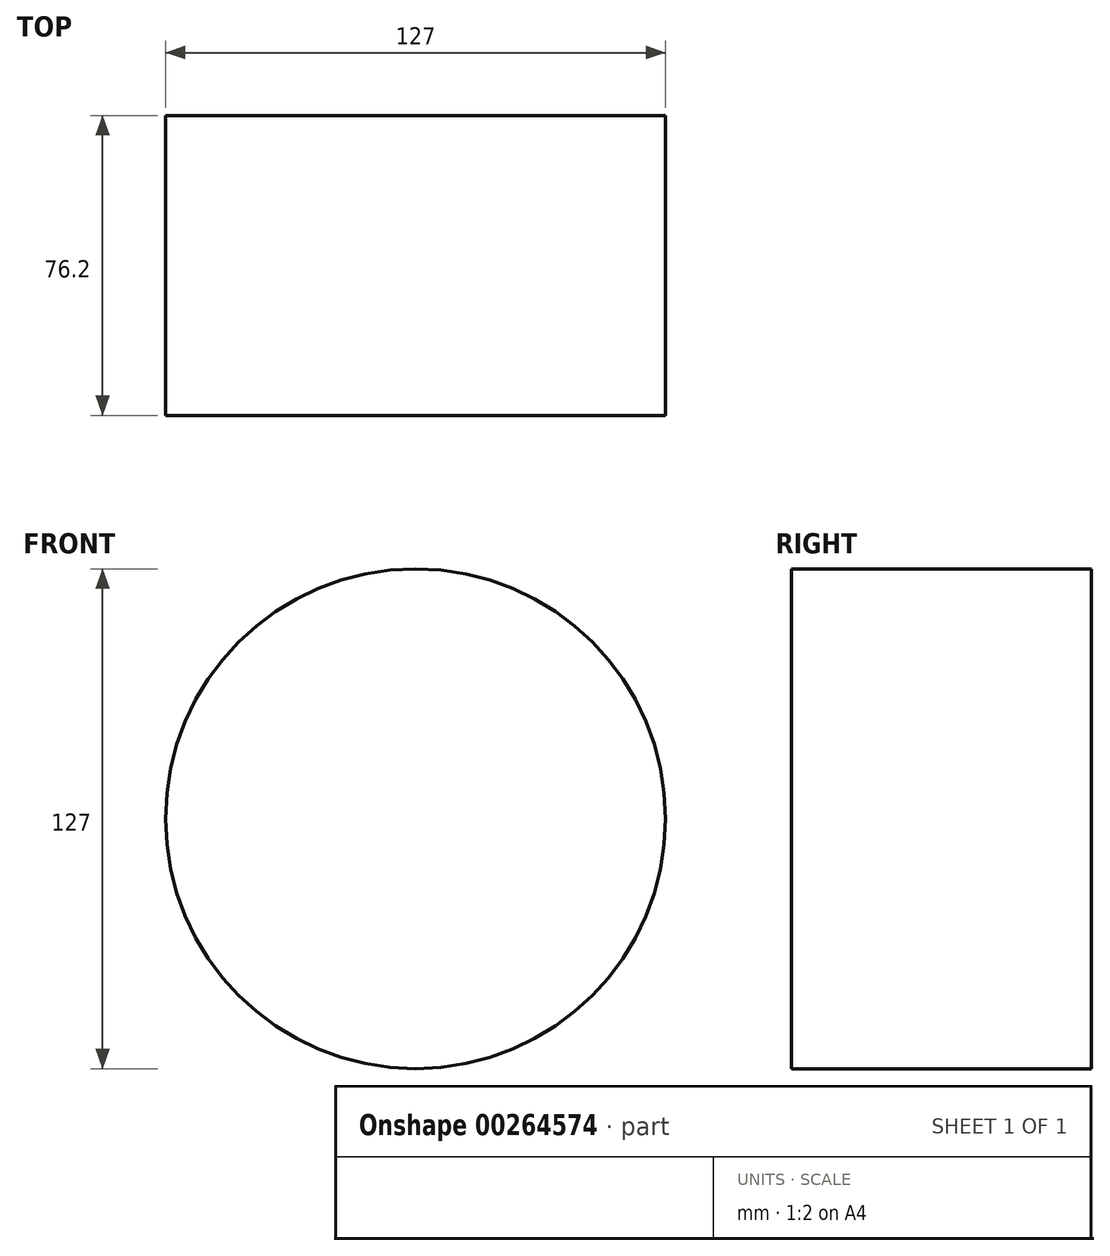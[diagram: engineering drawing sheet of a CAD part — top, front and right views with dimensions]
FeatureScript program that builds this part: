
annotation { "Feature Type Name" : "Feature", "Feature Type Description" : "" }
export const myFeature = defineFeature(function(context is Context, id is Id, definition is map)
    precondition{}
    {
        {
            var Q0;
            Q0=qCreatedBy(makeId("Front.planeOp"),FACE);
            var sketch = newSketch(context, id + "F0", { "sketchPlane" : qUnion([Q0])});
            skCircle(sketch, "E0", {"center": v(0, 0) * mm, "radius": 63.5 * mm});
            skSolve(sketch);
        }
        {
            var Q0;
            Q0 = qSketchRegion(id + "F0", true);
            extrude(context, id + "F1", {"entities" : qUnion([Q0]), "depth" : 76.2 * mm});
        }
    });
